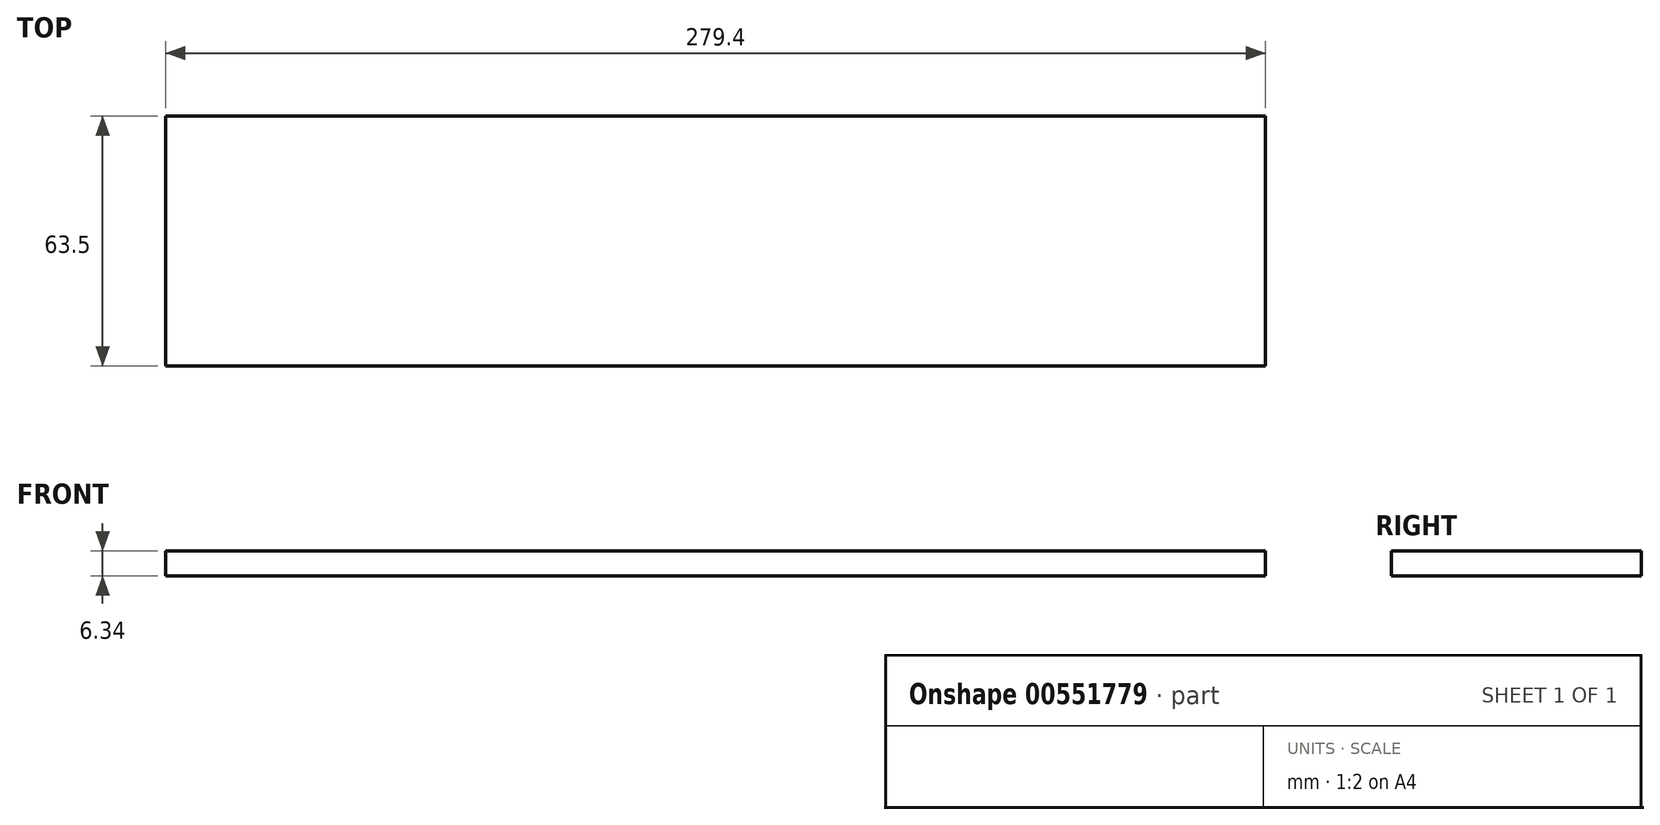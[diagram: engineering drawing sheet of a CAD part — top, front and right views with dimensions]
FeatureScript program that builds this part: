
annotation { "Feature Type Name" : "Feature", "Feature Type Description" : "" }
export const myFeature = defineFeature(function(context is Context, id is Id, definition is map)
    precondition{}
    {
        {
            var Q0;
            Q0=qCreatedBy(makeId("Top.planeOp"),FACE);
            var sketch = newSketch(context, id + "F0", { "sketchPlane" : qUnion([Q0])});
            skLineSegment(sketch, "E0.bottom", {"start": v(-139.7, 31.75) * mm, "end": v(139.7, 31.75) * mm});
            skLineSegment(sketch, "E0.top", {"start": v(-139.7, -31.75) * mm, "end": v(139.7, -31.75) * mm});
            skLineSegment(sketch, "E0.left", {"start": v(-139.7, 31.75) * mm, "end": v(-139.7, -31.75) * mm});
            skLineSegment(sketch, "E0.right", {"start": v(139.7, 31.75) * mm, "end": v(139.7, -31.75) * mm});
            skPoint(sketch, "E0.middle", {"position": v(0, 0) * mm});
            skSolve(sketch);
        }
        {
            var Q0;
            Q0=makeQuery(id+"F0.imprint","IMPRINT",FACE,{"disambiguationData":[TD([[makeQuery(id+"F0.imprint","IMPRINT",EDGE,{"derivedFrom":sQuery(id+"F0.wireOp",EDGE,"E0.bottom")}),-1.0]])]});
            extrude(context, id + "F1", {"entities" : qUnion([Q0]), "endBound" : BoundingType.SYMMETRIC, "depth" : 6.35 * mm, "offsetDistance" : 25.4 * mm});
        }
    });
